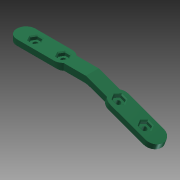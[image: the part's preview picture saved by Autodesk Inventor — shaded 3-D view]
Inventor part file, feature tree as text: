
AUTODESK INVENTOR PART (.ipt)
format: ipt  version: 2015 (Build 190159000, 159)  size: 261,120 bytes
history: native  units: in
note: dims shown in document units (in); Inventor stores cm internally (conversion verified against a paired STEP export)
features: extrude x6, sketch x6, plane x3, chamfer x1, mirror x1, fillet x1, projected_geometry x1
ambient origin geometry x8: Origin, YZ Plane, XZ Plane, XY Plane, X Axis, Y Axis, Z Axis, Center Point
bodies: Solid1 (feature_tree)
feature tree (19):
  extrude  "Extrusion1"  Depth=1.0in
  extrude  "Extrusion2"  Depth=0.1in
  extrude  "Extrusion3"  Depth=0.15in
  extrude  "Extrusion4"  Depth=0.25in
  extrude  "Extrusion5"  Depth=0.195in
  plane  "Work Plane2"
  extrude  "Extrusion6"  Depth=0.1in TaperAngle=0.0deg
  chamfer  "Chamfer1"  Distance=0.23in
  plane  "Work Plane4"
  mirror  "Mirror2"
  fillet  "Fillet3"  Radius=0.0984in
  sketch  "Sketch1"  dims[d0=0.297in d1=1.0in]
  sketch  "Sketch2"  dims[d2=0.1in d3=0.0in d4=0.1in]
  sketch  "Sketch3"  dims[d5=0.15in d6=0.0in d7=0.12in]
  sketch  "Sketch4"  dims[d8=0.75in d9=0.25in]
  sketch  "Sketch5"  dims[d10=0.1in d11=0.0in d12=0.195in]
  sketch  "Sketch6"  dims[d13=0.0975in d14=0.1in d15=0.0in d16=0.23in d17=0.0984in d18=0.0in d19=0.55in d20=0.05in d21=0.0in d22=0.0in d25=0.025in d26=0.125in d27=45.0deg d31=-0.0687in d32=0.5in]
  projected_geometry  "Projected Loop1"
  plane  "Work Plane5"
